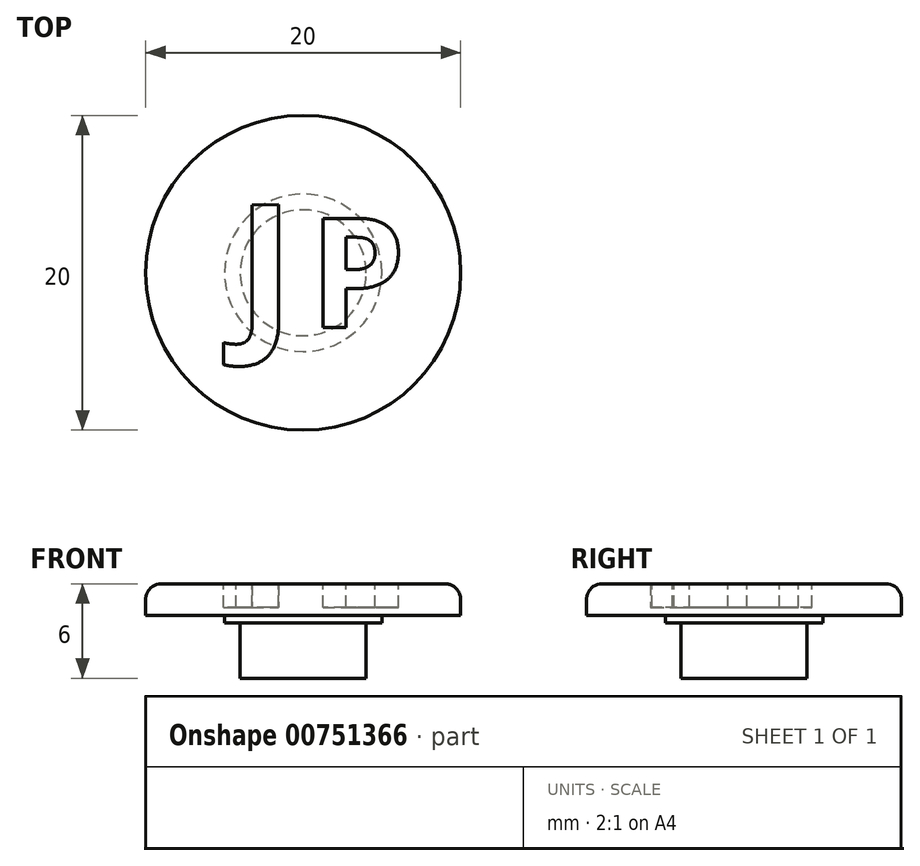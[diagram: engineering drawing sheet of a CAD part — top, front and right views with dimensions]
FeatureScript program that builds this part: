
annotation { "Feature Type Name" : "Feature", "Feature Type Description" : "" }
export const myFeature = defineFeature(function(context is Context, id is Id, definition is map)
    precondition{}
    {
        {
            var Q0;
            Q0=qCreatedBy(makeId("Top.planeOp"),FACE);
            var sketch = newSketch(context, id + "F0", { "sketchPlane" : qUnion([Q0])});
            skCircle(sketch, "E0", {"center": v(0, 0) * mm, "radius": 10 * mm});
            skCircle(sketch, "E1", {"center": v(0, 0) * mm, "radius": 4 * mm});
            skCircle(sketch, "E2", {"center": v(0, 0) * mm, "radius": 5 * mm});
            skSolve(sketch);
        }
        {
            var Q0;
            Q0=makeQuery(id+"F0.imprint","IMPRINT",FACE,{"disambiguationData":[TD([[makeQuery(id+"F0.imprint","IMPRINT",EDGE,{"derivedFrom":sQuery(id+"F0.wireOp",EDGE,"E1")}),1.0]])]});
            extrude(context, id + "F1", {"entities" : qUnion([Q0]), "oppositeDirection" : true, "depth" : 6 * mm, "offsetDistance" : 25 * mm});
        }
        {
            var Q0;
            Q0=makeQuery(id+"F0.imprint","IMPRINT",FACE,{"disambiguationData":[TD([[makeQuery(id+"F0.imprint","IMPRINT",EDGE,{"derivedFrom":sQuery(id+"F0.wireOp",EDGE,"E1")}),-1.0]])]});
            extrude(context, id + "F2", {"entities" : qUnion([Q0]), "operationType" : NewBodyOperationType.ADD, "oppositeDirection" : true, "depth" : 2.5 * mm, "offsetDistance" : 25 * mm});
        }
        {
            var Q0;
            Q0=makeQuery(id+"F0.imprint","IMPRINT",FACE,{"disambiguationData":[TD([[makeQuery(id+"F0.imprint","IMPRINT",EDGE,{"derivedFrom":sQuery(id+"F0.wireOp",EDGE,"E0")}),1.0]])]});
            extrude(context, id + "F3", {"entities" : qUnion([Q0]), "operationType" : NewBodyOperationType.ADD, "oppositeDirection" : true, "depth" : 2 * mm, "offsetDistance" : 25 * mm});
        }
        {
            var Q0;
            Q0=makeQuery(id+"F3.opExtrude","CAP_EDGE",EDGE,{"disambiguationData":[OSD([sQuery(id+"F0.wireOp",EDGE,"E0")])],"isStart":true});
            fillet(context, id + "F4", {"entities" : qUnion([Q0]), "radius" : 1 * mm, "tangentPropagation" : true, "allowEdgeOverflow" : false});
        }
        {
            var Q0;
            Q0=qCreatedBy(makeId("Top.planeOp"),FACE);
            var sketch = newSketch(context, id + "F5", { "sketchPlane" : qUnion([Q0])});
            skText(sketch, "E3", { "text": "J", "fontName": "OpenSans-Bold.ttf"});
            skText(sketch, "E4", { "text": "P", "fontName": "OpenSans-Bold.ttf"});
            skPoint(sketch, "E5", {"position": v(0.38, 0.02) * mm});
            skPoint(sketch, "E6", {"position": v(-0.01, 0.39) * mm});
            const initialGuessF5  = {"E3": [-0.00423, -0.00362, 1, 0.0028, 0.008], "E4": [0.00038, -0.00348, 1, 0, 0.007]};
            skSetInitialGuess(sketch, initialGuessF5);
            skSolve(sketch);
        }
        {
            var Q0;
            Q0=makeQuery(id+"F5.imprint","IMPRINT",FACE,{"disambiguationData":[TD([[makeQuery(id+"F5.imprint","IMPRINT",EDGE,{"derivedFrom":sQuery(id+"F5.wireOp",EDGE,"E3.sketch_text.stroke-0")}),-1.0]])]});
            var Q1;
            Q1=makeQuery(id+"F5.imprint","IMPRINT",FACE,{"disambiguationData":[TD([[makeQuery(id+"F5.imprint","IMPRINT",EDGE,{"derivedFrom":sQuery(id+"F5.wireOp",EDGE,"E4.sketch_text.stroke-0")}),-1.0]])]});
            extrude(context, id + "F6", {"entities" : qUnion([Q0, Q1]), "operationType" : NewBodyOperationType.REMOVE, "oppositeDirection" : true, "depth" : 1.5 * mm, "offsetDistance" : 25 * mm});
        }
    });
